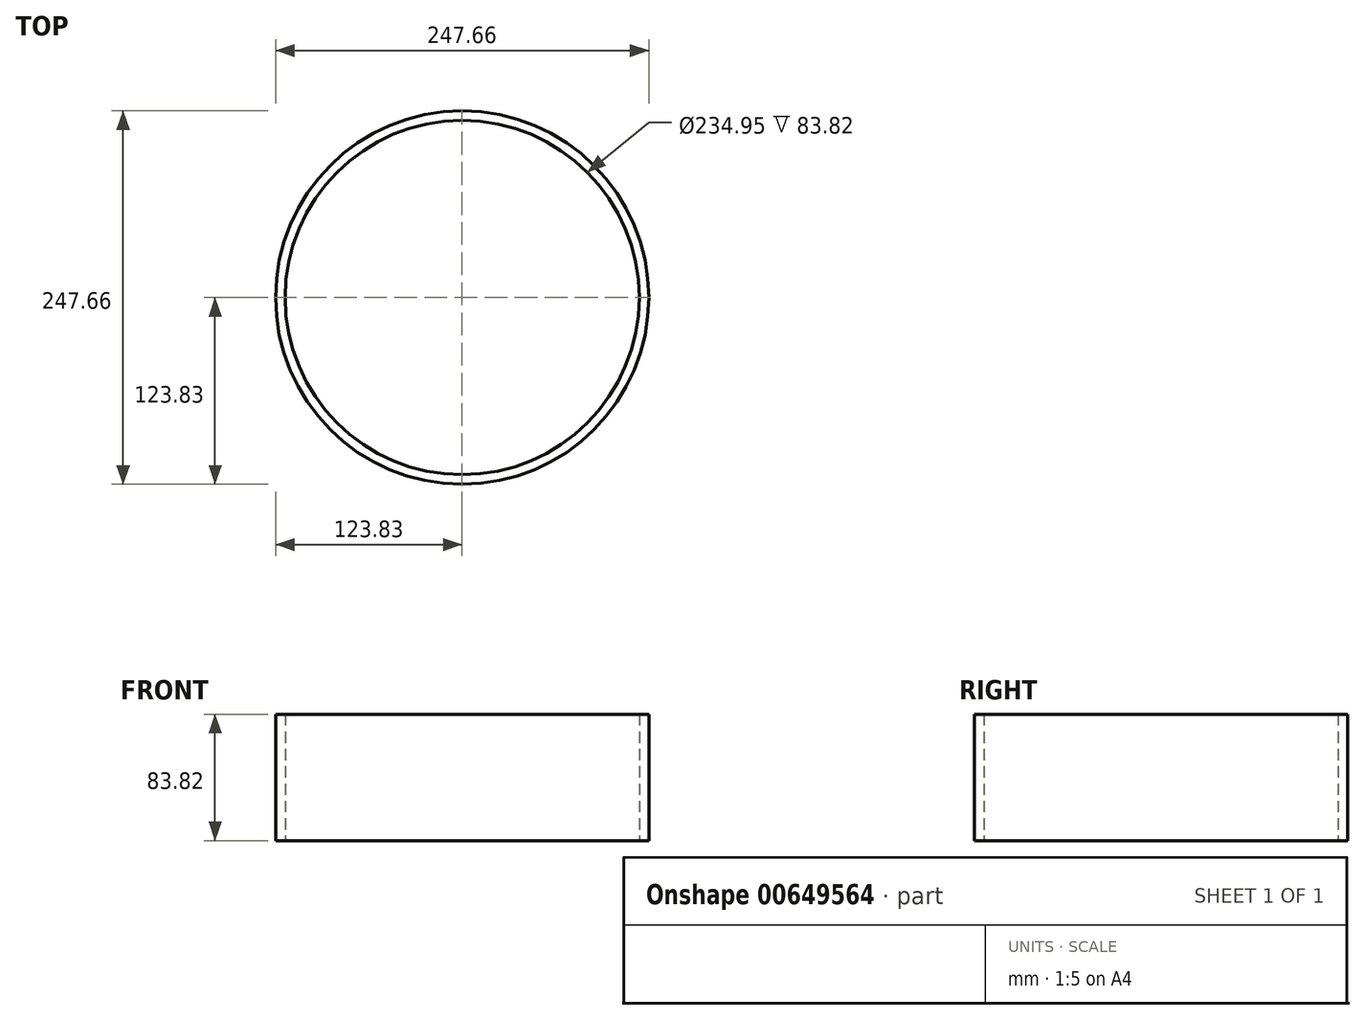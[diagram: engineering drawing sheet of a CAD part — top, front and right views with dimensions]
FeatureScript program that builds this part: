
annotation { "Feature Type Name" : "Feature", "Feature Type Description" : "" }
export const myFeature = defineFeature(function(context is Context, id is Id, definition is map)
    precondition{}
    {
        {
            var Q0;
            Q0=qCreatedBy(makeId("Top.planeOp"), FACE);
            var sketch = newSketch(context, id + "F0", { "sketchPlane" : qUnion([Q0])});
            skCircle(sketch, "E0", {"center": v(0, 0) * mm, "radius": 117.48 * mm});
            skCircle(sketch, "E1", {"center": v(0, 0) * mm, "radius": 123.83 * mm});
            skSolve(sketch);
        }
        {
            var Q0;
            Q0 = qSketchRegion(id + "F0", true);
            extrude(context, id + "F1", {"entities" : qUnion([Q0]), "depth" : 83.82 * mm, "offsetDistance" : 25.4 * mm});
        }
    });
